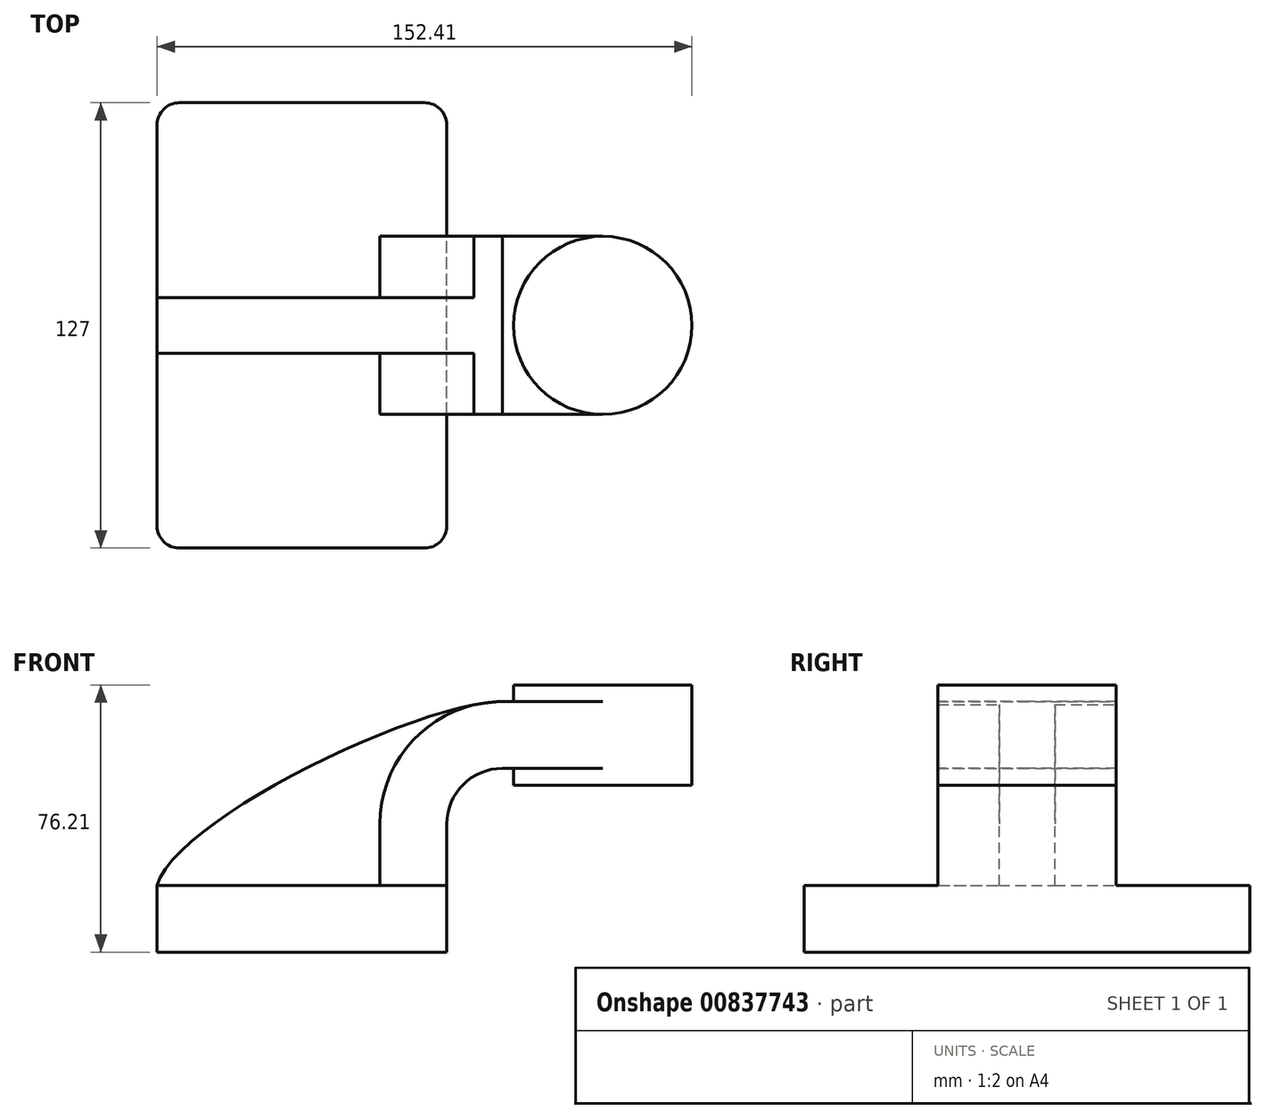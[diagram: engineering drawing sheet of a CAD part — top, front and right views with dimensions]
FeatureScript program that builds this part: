
annotation { "Feature Type Name" : "Feature", "Feature Type Description" : "" }
export const myFeature = defineFeature(function(context is Context, id is Id, definition is map)
    precondition{}
    {
        {
            var Q0;
            Q0=qCreatedBy(makeId("Front.planeOp"),FACE);
            var sketch = newSketch(context, id + "F0", { "sketchPlane" : qUnion([Q0])});
            skLineSegment(sketch, "E0.bottom", {"start": v(41.28, -9.52) * mm, "end": v(-41.28, -9.53) * mm});
            skLineSegment(sketch, "E0.top", {"start": v(41.28, 9.53) * mm, "end": v(-41.28, 9.53) * mm});
            skLineSegment(sketch, "E0.left", {"start": v(41.28, -9.52) * mm, "end": v(41.28, 9.53) * mm});
            skLineSegment(sketch, "E0.right", {"start": v(-41.28, -9.53) * mm, "end": v(-41.28, 9.53) * mm});
            skPoint(sketch, "E0.middle", {"position": v(0, 0) * mm});
            skLineSegment(sketch, "E1", {"start": v(41.28, 9.53) * mm, "end": v(41.28, 27) * mm});
            skArc(sketch, "E2", {"start": v(41.27, 27) * mm, "mid": v(45.92, 38.23) * mm, "end": v(57.15, 42.88) * mm});
            skLineSegment(sketch, "E3", {"start": v(57.15, 42.88) * mm, "end": v(85.72, 42.88) * mm});
            skLineSegment(sketch, "E4.bottom", {"start": v(111.12, 38.1) * mm, "end": v(60.32, 38.1) * mm});
            skLineSegment(sketch, "E4.top", {"start": v(111.12, 66.68) * mm, "end": v(60.32, 66.68) * mm});
            skLineSegment(sketch, "E4.left", {"start": v(111.12, 38.1) * mm, "end": v(111.12, 66.68) * mm});
            skLineSegment(sketch, "E4.right", {"start": v(60.32, 38.1) * mm, "end": v(60.32, 66.67) * mm});
            skPoint(sketch, "E4.middle", {"position": v(85.72, 52.39) * mm});
            skLineSegment(sketch, "E5.0", {"start": v(57.15, 61.93) * mm, "end": v(85.72, 61.93) * mm});
            skArc(sketch, "E5.1", {"start": v(22.23, 27) * mm, "mid": v(32.45, 51.7) * mm, "end": v(57.15, 61.93) * mm});
            skLineSegment(sketch, "E5.2", {"start": v(22.22, 9.53) * mm, "end": v(22.22, 27) * mm});
            skLineSegment(sketch, "E6", {"start": v(85.72, 38.1) * mm, "end": v(85.72, 42.88) * mm});
            skLineSegment(sketch, "E7", {"start": v(85.72, 42.88) * mm, "end": v(85.72, 61.93) * mm});
            skLineSegment(sketch, "E8", {"start": v(85.72, 61.93) * mm, "end": v(85.72, 66.68) * mm});
            skFitSpline(sketch, "E9", {"points": [v(-41.28, 9.52) * mm, v(57.15, 61.93) * mm], "startDerivative": vector(15.77, 56.05) * mm, "endDerivative": vector(74.33, 1.17) * mm});
            skSolve(sketch);
        }
        {
            var Q0;
            Q0=makeQuery(id+"F0.imprint","IMPRINT",FACE,{"disambiguationData":[TD([[makeQuery(id+"F0.imprint","IMPRINT",EDGE,{"derivedFrom":sQuery(id+"F0.wireOp",EDGE,"E0.bottom")}),-1.0]])]});
            extrude(context, id + "F1", {"entities" : qUnion([Q0]), "endBound" : BoundingType.SYMMETRIC, "depth" : 127 * mm, "offsetDistance" : 25.4 * mm});
        }
        {
            var Q0;
            {var subQ4=sQuery(id+"F0.wireOp",EDGE,"E1");Q0=makeQuery(id+"F0.imprint","IMPRINT",FACE,{"disambiguationData":[TD([[makeQuery(id+"F0.imprint","IMPRINT",EDGE,{"derivedFrom":subQ4}),1.0]])]});}
            var Q1;
            {var subQ0=sQuery(id+"F0.wireOp",EDGE,"E7");Q1=makeQuery(id+"F0.imprint","IMPRINT",FACE,{"disambiguationData":[TD([[makeQuery(id+"F0.imprint","IMPRINT",EDGE,{"derivedFrom":subQ0}),1.0]])]});}
            extrude(context, id + "F2", {"entities" : qUnion([Q0, Q1]), "operationType" : NewBodyOperationType.ADD, "endBound" : BoundingType.SYMMETRIC, "depth" : 50.8 * mm, "offsetDistance" : 25.4 * mm});
        }
        {
            var Q0;
            {var subQ3=sQuery(id+"F0.wireOp",EDGE,"E5.2");Q0=makeQuery(id+"F0.imprint","IMPRINT",FACE,{"disambiguationData":[TD([[makeQuery(id+"F0.imprint","IMPRINT",EDGE,{"derivedFrom":subQ3}),1.0]])]});}
            extrude(context, id + "F3", {"entities" : qUnion([Q0]), "operationType" : NewBodyOperationType.ADD, "endBound" : BoundingType.SYMMETRIC, "depth" : 15.88 * mm, "offsetDistance" : 25.4 * mm});
        }
        {
            var Q0;
            {var subQ1=sQuery(id+"F0.wireOp",EDGE,"E4.left");Q0=makeQuery(id+"F0.imprint","IMPRINT",FACE,{"disambiguationData":[TD([[makeQuery(id+"F0.imprint","IMPRINT",EDGE,{"derivedFrom":subQ1}),1.0]])]});}
            var Q1;
            Q1=sQuery(id+"F0.wireOp",EDGE,"E7");
            revolve(context, id + "F4", {"operationType" : NewBodyOperationType.ADD, "surfaceOperationType" : NewSurfaceOperationType.NEW, "entities" : qUnion([Q0]), "axis" : qUnion([Q1]), "revolveType" : RevolveType.FULL});
        }
        {
            var Q0;
            Q0=makeQuery(id+"F1.opExtrude","CAP_EDGE",EDGE,{"disambiguationData":[OSD([sQuery(id+"F0.wireOp",EDGE,"E0.left")])],"isStart":false});
            var Q1;
            Q1=makeQuery(id+"F1.opExtrude","CAP_EDGE",EDGE,{"disambiguationData":[OSD([sQuery(id+"F0.wireOp",EDGE,"E0.right")])],"isStart":false});
            var Q2;
            Q2=makeQuery(id+"F1.opExtrude","CAP_EDGE",EDGE,{"disambiguationData":[OSD([sQuery(id+"F0.wireOp",EDGE,"E0.left")])],"isStart":true});
            var Q3;
            Q3=makeQuery(id+"F1.opExtrude","CAP_EDGE",EDGE,{"disambiguationData":[OSD([sQuery(id+"F0.wireOp",EDGE,"E0.right")])],"isStart":true});
            fillet(context, id + "F5", {"entities" : qUnion([Q0, Q1, Q2, Q3]), "radius" : 6.35 * mm, "tangentPropagation" : true, "allowEdgeOverflow" : false});
        }
    });
